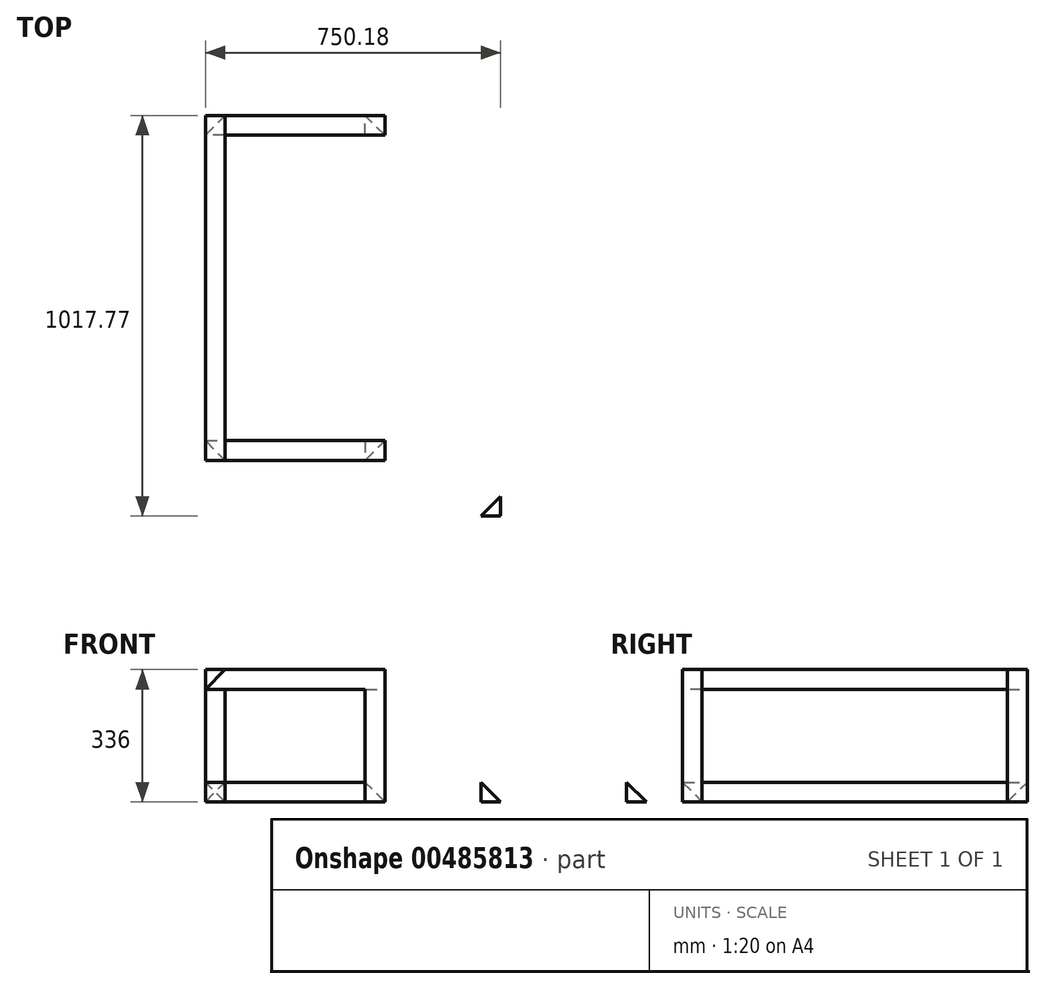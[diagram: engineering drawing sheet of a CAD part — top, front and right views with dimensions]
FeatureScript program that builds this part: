
annotation { "Feature Type Name" : "Feature", "Feature Type Description" : "" }
export const myFeature = defineFeature(function(context is Context, id is Id, definition is map)
    precondition{}
    {
        {
            var Q0;
            Q0=qCreatedBy(makeId("Top.planeOp"),FACE);
            var sketch = newSketch(context, id + "F0", { "sketchPlane" : qUnion([Q0])});
            skLineSegment(sketch, "E0.bottom", {"start": v(-25, 388) * mm, "end": v(25, 388) * mm});
            skLineSegment(sketch, "E0.top", {"start": v(-25, -388) * mm, "end": v(25, -388) * mm});
            skLineSegment(sketch, "E0.left", {"start": v(-25, 388) * mm, "end": v(-25, -388) * mm});
            skLineSegment(sketch, "E0.right", {"start": v(25, 388) * mm, "end": v(25, -388) * mm});
            skPoint(sketch, "E0.middle", {"position": v(0, 0) * mm});
            skSolve(sketch);
        }
        {
            var Q0;
            Q0 = qSketchRegion(id + "F0", true);
            extrude(context, id + "F1", {"entities" : qUnion([Q0]), "depth" : 50 * mm});
        }
        {
            var Q0;
            Q0=makeQuery(id+"F1.opExtrude","CAP_FACE",FACE,{"disambiguationData":[OSD([sQuery(id+"F0.wireOp",EDGE,"E0.bottom"),sQuery(id+"F0.wireOp",EDGE,"E0.top"),sQuery(id+"F0.wireOp",EDGE,"E0.left"),sQuery(id+"F0.wireOp",EDGE,"E0.right")])],"isStart":false});
            var sketch = newSketch(context, id + "F2", { "sketchPlane" : qUnion([Q0])});
            skLineSegment(sketch, "E1.top", {"start": v(-25, -438) * mm, "end": v(25, -438) * mm});
            skLineSegment(sketch, "E1.left", {"start": v(-25, -388) * mm, "end": v(-25, -438) * mm});
            skLineSegment(sketch, "E2.top", {"start": v(-25, 438) * mm, "end": v(25, 438) * mm});
            skLineSegment(sketch, "E2.left", {"start": v(-25, 388) * mm, "end": v(-25, 438) * mm});
            skLineSegment(sketch, "E3", {"start": v(25, -438) * mm, "end": v(-25, -388) * mm});
            skLineSegment(sketch, "E4", {"start": v(-25, 388) * mm, "end": v(25, 438) * mm});
            skSolve(sketch);
        }
        {
            var Q0;
            Q0 = qSketchRegion(id + "F2", true);
            extrude(context, id + "F3", {"entities" : qUnion([Q0]), "depth" : 236 * mm, "offsetDistance" : 25 * mm});
        }
        {
            var Q0;
            Q0=makeQuery(id+"F1.opExtrude","SWEPT_FACE",FACE,{"disambiguationData":[OSD([sQuery(id+"F0.wireOp",EDGE,"E0.right")])]});
            var sketch = newSketch(context, id + "F4", { "sketchPlane" : qUnion([Q0])});
            skLineSegment(sketch, "E5.bottom", {"start": v(-388, 0) * mm, "end": v(-438, 0) * mm});
            skLineSegment(sketch, "E5.right", {"start": v(-438, 0) * mm, "end": v(-438, 50) * mm});
            skLineSegment(sketch, "E6.bottom", {"start": v(388, 0) * mm, "end": v(438, 0) * mm});
            skLineSegment(sketch, "E6.right", {"start": v(438, 0) * mm, "end": v(438, 50) * mm});
            skLineSegment(sketch, "E7", {"start": v(-438, 50) * mm, "end": v(-388, 0) * mm});
            skLineSegment(sketch, "E8", {"start": v(388, 0) * mm, "end": v(438, 50) * mm});
            skSolve(sketch);
        }
        {
            var Q0;
            Q0 = qSketchRegion(id + "F4", true);
            extrude(context, id + "F5", {"entities" : qUnion([Q0]), "depth" : 356 * mm});
        }
        {
            var Q0;
            Q0=makeQuery(id+"F1.opExtrude","SWEPT_FACE",FACE,{"disambiguationData":[OSD([sQuery(id+"F0.wireOp",EDGE,"E0.bottom")])]});
            var sketch = newSketch(context, id + "F6", { "sketchPlane" : qUnion([Q0])});
            skLineSegment(sketch, "E9", {"start": v(-25, 0) * mm, "end": v(25, 50) * mm});
            skLineSegment(sketch, "E10", {"start": v(25, 50) * mm, "end": v(-25, 50) * mm});
            skLineSegment(sketch, "E11", {"start": v(-25, 50) * mm, "end": v(-25, 0) * mm});
            skSolve(sketch);
        }
        {
            var Q0;
            Q0=makeQuery(id+"F6.imprint","IMPRINT",FACE,{"disambiguationData":[TD([[makeQuery(id+"F6.imprint","IMPRINT",EDGE,{"derivedFrom":sQuery(id+"F6.wireOp",EDGE,"E9")}),1.0]])]});
            extrude(context, id + "F7", {"entities" : qUnion([Q0]), "operationType" : NewBodyOperationType.REMOVE, "oppositeDirection" : true, "depth" : 800 * mm});
        }
        {
            var Q0;
            Q0=makeQuery(id+"F5.opExtrude","SWEPT_FACE",FACE,{"disambiguationData":[OSD([sQuery(id+"F4.wireOp",EDGE,"E5.bottom")])]});
            var sketch = newSketch(context, id + "F8", { "sketchPlane" : qUnion([Q0])});
            skLineSegment(sketch, "E12.bottom", {"start": v(381, 438) * mm, "end": v(431, 438) * mm});
            skLineSegment(sketch, "E12.right", {"start": v(431, 438) * mm, "end": v(431, 388) * mm});
            skLineSegment(sketch, "E13", {"start": v(381, 438) * mm, "end": v(431, 388) * mm});
            skSolve(sketch);
        }
        {
            var Q0;
            Q0 = qSketchRegion(id + "F8", true);
            var Q1;
            Q1=makeQuery(id+"F3.opExtrude","CAP_FACE",FACE,{"disambiguationData":[OSD([sQuery(id+"F2.wireOp",EDGE,"E1.top"),sQuery(id+"F2.wireOp",EDGE,"E1.left"),sQuery(id+"F2.wireOp",EDGE,"E3")])],"isStart":false});
            extrude(context, id + "F9", {"entities" : qUnion([Q0]), "endBound" : BoundingType.UP_TO_SURFACE, "oppositeDirection" : true, "endBoundEntityFace" : qUnion([Q1]), "depth" : 25 * mm});
        }
        {
            var Q0;
            Q0=makeQuery(id+"F5.opExtrude","SWEPT_FACE",FACE,{"disambiguationData":[OSD([sQuery(id+"F4.wireOp",EDGE,"E6.bottom")])]});
            var sketch = newSketch(context, id + "F10", { "sketchPlane" : qUnion([Q0])});
            skLineSegment(sketch, "E14.bottom", {"start": v(381, -438) * mm, "end": v(431, -438) * mm});
            skLineSegment(sketch, "E14.right", {"start": v(431, -438) * mm, "end": v(431, -388) * mm});
            skLineSegment(sketch, "E15", {"start": v(381, -438) * mm, "end": v(431, -388) * mm});
            skSolve(sketch);
        }
        {
            var Q0;
            Q0 = qSketchRegion(id + "F10", true);
            var Q1;
            Q1=makeQuery(id+"F3.opExtrude","CAP_FACE",FACE,{"disambiguationData":[OSD([sQuery(id+"F2.wireOp",EDGE,"E2.top"),sQuery(id+"F2.wireOp",EDGE,"E2.left"),sQuery(id+"F2.wireOp",EDGE,"E4")])],"isStart":false});
            extrude(context, id + "F11", {"entities" : qUnion([Q0]), "endBound" : BoundingType.UP_TO_SURFACE, "oppositeDirection" : true, "endBoundEntityFace" : qUnion([Q1]), "depth" : 25 * mm});
        }
        {
            var Q0;
            Q0=makeQuery(id+"F3.opExtrude","CAP_FACE",FACE,{"disambiguationData":[OSD([sQuery(id+"F2.wireOp",EDGE,"E1.top"),sQuery(id+"F2.wireOp",EDGE,"E1.left"),sQuery(id+"F2.wireOp",EDGE,"E3")])],"isStart":false});
            var sketch = newSketch(context, id + "F12", { "sketchPlane" : qUnion([Q0])});
            skLineSegment(sketch, "E16.bottom", {"start": v(-25, -438) * mm, "end": v(25, -438) * mm});
            skLineSegment(sketch, "E16.top", {"start": v(-25, 438) * mm, "end": v(25, 438) * mm});
            skLineSegment(sketch, "E16.left", {"start": v(-25, -438) * mm, "end": v(-25, 438) * mm});
            skLineSegment(sketch, "E16.right", {"start": v(25, -438) * mm, "end": v(25, 438) * mm});
            skSolve(sketch);
        }
        {
            var Q0;
            Q0 = qSketchRegion(id + "F12", true);
            extrude(context, id + "F13", {"entities" : qUnion([Q0]), "depth" : 50 * mm});
        }
        {
            var Q0;
            Q0=makeQuery(id+"F13.opExtrude","SWEPT_FACE",FACE,{"disambiguationData":[OSD([sQuery(id+"F12.wireOp",EDGE,"E16.bottom")])]});
            var sketch = newSketch(context, id + "F14", { "sketchPlane" : qUnion([Q0])});
            skLineSegment(sketch, "E17", {"start": v(-25, 286) * mm, "end": v(25, 336) * mm});
            skLineSegment(sketch, "E18", {"start": v(-25, 286) * mm, "end": v(25, 286) * mm});
            skLineSegment(sketch, "E19", {"start": v(25, 286) * mm, "end": v(25, 336) * mm});
            skSolve(sketch);
        }
        {
            var Q0;
            Q0 = qSketchRegion(id + "F14", true);
            extrude(context, id + "F15", {"entities" : qUnion([Q0]), "operationType" : NewBodyOperationType.REMOVE, "oppositeDirection" : true, "depth" : 880 * mm});
        }
        {
            var Q0;
            Q0=makeQuery(id+"F11.opExtrude","SWEPT_FACE",FACE,{"disambiguationData":[OSD([sQuery(id+"F10.wireOp",EDGE,"E14.bottom")])]});
            var sketch = newSketch(context, id + "F16", { "sketchPlane" : qUnion([Q0])});
            skLineSegment(sketch, "E20", {"start": v(-431, 286) * mm, "end": v(-381, 286) * mm});
            skLineSegment(sketch, "E21", {"start": v(-381, 286) * mm, "end": v(-381, 336) * mm});
            skLineSegment(sketch, "E22", {"start": v(-381, 336) * mm, "end": v(-431, 286) * mm});
            skSolve(sketch);
        }
        {
            var Q0;
            Q0 = qSketchRegion(id + "F16", true);
            extrude(context, id + "F17", {"entities" : qUnion([Q0]), "oppositeDirection" : true, "depth" : 50 * mm});
        }
        {
            var Q0;
            Q0=makeQuery(id+"F17.opExtrude","SWEPT_FACE",FACE,{"disambiguationData":[OSD([sQuery(id+"F16.wireOp",EDGE,"E21")])]});
            extrude(context, id + "F18", {"entities" : qUnion([Q0]), "endBound" : BoundingType.UP_TO_NEXT, "depth" : 25 * mm});
        }
        {
            var Q0;
            Q0=makeQuery(id+"F17.opExtrude","SWEPT_BODY",BODY,{"disambiguationData":[OSD([sQuery(id+"F16.wireOp",EDGE,"E20"),sQuery(id+"F16.wireOp",EDGE,"E21"),sQuery(id+"F16.wireOp",EDGE,"E22")])]});
            var Q1;
            Q1=makeQuery(id+"F18.opExtrude","SWEPT_BODY",BODY,{"disambiguationData":[OSD([sQuery(id+"F16.wireOp",EDGE,"E21")])]});
            booleanBodies(context, id + "F19", {"operationType" : BooleanOperationType.UNION, "tools" : qUnion([Q0, Q1])});
        }
        {
            var Q0;
            Q0=makeQuery(id+"F9.opExtrude","SWEPT_FACE",FACE,{"disambiguationData":[OSD([sQuery(id+"F8.wireOp",EDGE,"E12.bottom")])]});
            var sketch = newSketch(context, id + "F20", { "sketchPlane" : qUnion([Q0])});
            skLineSegment(sketch, "E23", {"start": v(431, 286) * mm, "end": v(381, 286) * mm});
            skLineSegment(sketch, "E24", {"start": v(381, 286) * mm, "end": v(381, 336) * mm});
            skLineSegment(sketch, "E25", {"start": v(381, 336) * mm, "end": v(431, 286) * mm});
            skSolve(sketch);
        }
        {
            var Q0;
            Q0 = qSketchRegion(id + "F20", true);
            extrude(context, id + "F21", {"entities" : qUnion([Q0]), "oppositeDirection" : true, "depth" : 50 * mm});
        }
        {
            var Q0;
            Q0=makeQuery(id+"F21.opExtrude","SWEPT_FACE",FACE,{"disambiguationData":[OSD([sQuery(id+"F20.wireOp",EDGE,"E24")])]});
            extrude(context, id + "F22", {"entities" : qUnion([Q0]), "endBound" : BoundingType.UP_TO_NEXT, "depth" : 25 * mm});
        }
        {
            var Q0;
            Q0=makeQuery(id+"F21.opExtrude","SWEPT_BODY",BODY,{"disambiguationData":[OSD([sQuery(id+"F20.wireOp",EDGE,"E23"),sQuery(id+"F20.wireOp",EDGE,"E24"),sQuery(id+"F20.wireOp",EDGE,"E25")])]});
            var Q1;
            Q1=makeQuery(id+"F22.opExtrude","SWEPT_BODY",BODY,{"disambiguationData":[OSD([sQuery(id+"F20.wireOp",EDGE,"E24")])]});
            booleanBodies(context, id + "F23", {"operationType" : BooleanOperationType.UNION, "tools" : qUnion([Q0, Q1])});
        }
        {
            var Q0;
            Q0=makeQuery(id+"F5.opExtrude","CAP_FACE",FACE,{"disambiguationData":[OSD([sQuery(id+"F4.wireOp",EDGE,"E6.bottom"),sQuery(id+"F4.wireOp",EDGE,"E6.right"),sQuery(id+"F4.wireOp",EDGE,"E8")])],"isStart":false});
            var Q1;
            Q1=makeQuery(id+"F5.opExtrude","CAP_FACE",FACE,{"disambiguationData":[OSD([sQuery(id+"F4.wireOp",EDGE,"E5.bottom"),sQuery(id+"F4.wireOp",EDGE,"E5.right"),sQuery(id+"F4.wireOp",EDGE,"E7")])],"isStart":false});
            extrude(context, id + "F24", {"entities" : qUnion([Q0, Q1]), "endBound" : BoundingType.UP_TO_NEXT, "depth" : 25 * mm});
        }
        {
            var Q0;
            Q0=makeQuery(id+"F3.opExtrude","CAP_FACE",FACE,{"disambiguationData":[OSD([sQuery(id+"F2.wireOp",EDGE,"E2.top"),sQuery(id+"F2.wireOp",EDGE,"E2.left"),sQuery(id+"F2.wireOp",EDGE,"E4")])],"isStart":true});
            var Q1;
            Q1=makeQuery(id+"F3.opExtrude","CAP_FACE",FACE,{"disambiguationData":[OSD([sQuery(id+"F2.wireOp",EDGE,"E1.top"),sQuery(id+"F2.wireOp",EDGE,"E1.left"),sQuery(id+"F2.wireOp",EDGE,"E3")])],"isStart":true});
            var Q2;
            Q2=makeQuery(id+"F1.opExtrude","CAP_FACE",FACE,{"disambiguationData":[OSD([sQuery(id+"F0.wireOp",EDGE,"E0.bottom"),sQuery(id+"F0.wireOp",EDGE,"E0.top"),sQuery(id+"F0.wireOp",EDGE,"E0.left"),sQuery(id+"F0.wireOp",EDGE,"E0.right")])],"isStart":true});
            extrude(context, id + "F25", {"entities" : qUnion([Q0, Q1]), "endBound" : BoundingType.UP_TO_SURFACE, "endBoundEntityFace" : qUnion([Q2]), "depth" : 25 * mm});
        }
        {
            var Q0;
            Q0=makeQuery(id+"F5.opExtrude","CAP_FACE",FACE,{"disambiguationData":[OSD([sQuery(id+"F4.wireOp",EDGE,"E5.bottom"),sQuery(id+"F4.wireOp",EDGE,"E5.right"),sQuery(id+"F4.wireOp",EDGE,"E7")])],"isStart":true});
            var Q1;
            Q1=makeQuery(id+"F5.opExtrude","CAP_FACE",FACE,{"disambiguationData":[OSD([sQuery(id+"F4.wireOp",EDGE,"E6.bottom"),sQuery(id+"F4.wireOp",EDGE,"E6.right"),sQuery(id+"F4.wireOp",EDGE,"E8")])],"isStart":true});
            extrude(context, id + "F26", {"entities" : qUnion([Q0, Q1]), "endBound" : BoundingType.UP_TO_NEXT, "depth" : 25 * mm});
        }
        {
            var Q0;
            {var subQ0=sQuery(id+"F20.wireOp",EDGE,"E24");Q0=makeQuery(id+"F23.opBoolean","MERGE",FACE,{"derivedFrom":[makeQuery(id+"F21.opExtrude","CAP_FACE",FACE,{"disambiguationData":[OSD([sQuery(id+"F20.wireOp",EDGE,"E23"),subQ0,sQuery(id+"F20.wireOp",EDGE,"E25")])],"isStart":true}),makeQuery(id+"F22.opExtrude","SWEPT_FACE",FACE,{"disambiguationData":[OSD([subQ0]),TDD([makeQuery(id+"F21.opExtrude","CAP_EDGE",EDGE,{"disambiguationData":[OSD([subQ0])],"isStart":true})])]})]});}
            var sketch = newSketch(context, id + "F27", { "sketchPlane" : qUnion([Q0])});
            skLineSegment(sketch, "E26", {"start": v(381, 336) * mm, "end": v(431, 286) * mm});
            skLineSegment(sketch, "E27", {"start": v(431, 286) * mm, "end": v(431, 336) * mm});
            skLineSegment(sketch, "E28", {"start": v(431, 336) * mm, "end": v(381, 336) * mm});
            skSolve(sketch);
        }
        {
            var Q0;
            Q0 = qSketchRegion(id + "F27", true);
            var Q1;
            {var subQ0=sQuery(id+"F20.wireOp",EDGE,"E24");Q1=makeQuery(id+"F23.opBoolean","MERGE",FACE,{"derivedFrom":[makeQuery(id+"F21.opExtrude","CAP_FACE",FACE,{"disambiguationData":[OSD([sQuery(id+"F20.wireOp",EDGE,"E23"),subQ0,sQuery(id+"F20.wireOp",EDGE,"E25")])],"isStart":false}),makeQuery(id+"F22.opExtrude","SWEPT_FACE",FACE,{"disambiguationData":[OSD([subQ0]),TDD([makeQuery(id+"F21.opExtrude","CAP_EDGE",EDGE,{"disambiguationData":[OSD([subQ0])],"isStart":false})])]})]});}
            extrude(context, id + "F28", {"entities" : qUnion([Q0]), "operationType" : NewBodyOperationType.ADD, "endBound" : BoundingType.UP_TO_SURFACE, "oppositeDirection" : true, "depth" : 25 * mm, "endBoundEntityFace" : qUnion([Q1]), "offsetDistance" : 25 * mm});
        }
        {
            var Q0;
            {var subQ0=sQuery(id+"F16.wireOp",EDGE,"E21");Q0=makeQuery(id+"F19.opBoolean","MERGE",FACE,{"derivedFrom":[makeQuery(id+"F17.opExtrude","CAP_FACE",FACE,{"disambiguationData":[OSD([sQuery(id+"F16.wireOp",EDGE,"E20"),subQ0,sQuery(id+"F16.wireOp",EDGE,"E22")])],"isStart":true}),makeQuery(id+"F18.opExtrude","SWEPT_FACE",FACE,{"disambiguationData":[OSD([subQ0]),TDD([makeQuery(id+"F17.opExtrude","CAP_EDGE",EDGE,{"disambiguationData":[OSD([subQ0])],"isStart":true})])]})]});}
            var sketch = newSketch(context, id + "F29", { "sketchPlane" : qUnion([Q0])});
            skLineSegment(sketch, "E29", {"start": v(-431, 286) * mm, "end": v(-431, 336) * mm});
            skLineSegment(sketch, "E30", {"start": v(-431, 336) * mm, "end": v(-381, 336) * mm});
            skLineSegment(sketch, "E31", {"start": v(-381, 336) * mm, "end": v(-431, 286) * mm});
            skSolve(sketch);
        }
        {
            var Q0;
            Q0 = qSketchRegion(id + "F29", true);
            var Q1;
            {var subQ0=sQuery(id+"F16.wireOp",EDGE,"E21");Q1=makeQuery(id+"F19.opBoolean","MERGE",FACE,{"derivedFrom":[makeQuery(id+"F17.opExtrude","CAP_FACE",FACE,{"disambiguationData":[OSD([sQuery(id+"F16.wireOp",EDGE,"E20"),subQ0,sQuery(id+"F16.wireOp",EDGE,"E22")])],"isStart":false}),makeQuery(id+"F18.opExtrude","SWEPT_FACE",FACE,{"disambiguationData":[OSD([subQ0]),TDD([makeQuery(id+"F17.opExtrude","CAP_EDGE",EDGE,{"disambiguationData":[OSD([subQ0])],"isStart":false})])]})]});}
            extrude(context, id + "F30", {"entities" : qUnion([Q0]), "operationType" : NewBodyOperationType.ADD, "endBound" : BoundingType.UP_TO_SURFACE, "oppositeDirection" : true, "depth" : 25 * mm, "endBoundEntityFace" : qUnion([Q1]), "offsetDistance" : 25 * mm});
        }
        {
            var Q0;
            Q0=qCreatedBy(makeId("Top.planeOp"),FACE);
            var sketch = newSketch(context, id + "F31", { "sketchPlane" : qUnion([Q0])});
            skLineSegment(sketch, "E32.bottom", {"start": v(675.18, -579.77) * mm, "end": v(725.18, -579.77) * mm});
            skLineSegment(sketch, "E32.top", {"start": v(675.18, -529.77) * mm, "end": v(725.18, -529.77) * mm});
            skLineSegment(sketch, "E32.left", {"start": v(675.18, -579.77) * mm, "end": v(675.18, -529.77) * mm});
            skLineSegment(sketch, "E32.right", {"start": v(725.18, -579.77) * mm, "end": v(725.18, -529.77) * mm});
            skLineSegment(sketch, "E33", {"start": v(675.18, -579.77) * mm, "end": v(725.18, -529.77) * mm});
            skLineSegment(sketch, "E34", {"start": v(725.18, -579.77) * mm, "end": v(675.18, -579.77) * mm, "construction": true});
            skLineSegment(sketch, "E35", {"start": v(675.18, -529.77) * mm, "end": v(725.18, -529.77) * mm, "construction": true});
            skSolve(sketch);
        }
        {
            var Q0;
            Q0 = qSketchRegion(id + "F31", true);
            extrude(context, id + "F32", {"entities" : qUnion([Q0]), "depth" : 50 * mm, "offsetDistance" : 25 * mm});
        }
        {
            var Q0;
            Q0=makeQuery(id+"F32.opExtrude","SWEPT_FACE",FACE,{"disambiguationData":[OSD([sQuery(id+"F31.wireOp",EDGE,"E32.top")])]});
            var sketch = newSketch(context, id + "F33", { "sketchPlane" : qUnion([Q0])});
            skLineSegment(sketch, "E36", {"start": v(-675.18, 50) * mm, "end": v(-725.18, 50) * mm});
            skLineSegment(sketch, "E37", {"start": v(-725.18, 50) * mm, "end": v(-725.18, 0) * mm});
            skLineSegment(sketch, "E38", {"start": v(-725.18, 0) * mm, "end": v(-675.18, 50) * mm});
            skSolve(sketch);
        }
        {
            var Q0;
            Q0=makeQuery(id+"F32.opExtrude","CAP_FACE",FACE,{"disambiguationData":[OSD([sQuery(id+"F31.wireOp",EDGE,"E32.bottom"),sQuery(id+"F31.wireOp",EDGE,"E32.top"),sQuery(id+"F31.wireOp",EDGE,"E32.left"),sQuery(id+"F31.wireOp",EDGE,"E32.right")])],"isStart":false});
            var sketch = newSketch(context, id + "F34", { "sketchPlane" : qUnion([Q0])});
            skLineSegment(sketch, "E39", {"start": v(675.18, -579.77) * mm, "end": v(725.18, -529.77) * mm});
            skLineSegment(sketch, "E40", {"start": v(725.18, -529.77) * mm, "end": v(675.18, -529.77) * mm});
            skLineSegment(sketch, "E41", {"start": v(675.18, -529.77) * mm, "end": v(675.18, -579.77) * mm});
            skSolve(sketch);
        }
        {
            var Q0;
            Q0 = qSketchRegion(id + "F34", true);
            extrude(context, id + "F35", {"entities" : qUnion([Q0]), "operationType" : NewBodyOperationType.REMOVE, "oppositeDirection" : true, "depth" : 50 * mm, "offsetDistance" : 25 * mm});
        }
        {
            var Q0;
            Q0 = qSketchRegion(id + "F33", true);
            extrude(context, id + "F36", {"entities" : qUnion([Q0]), "operationType" : NewBodyOperationType.REMOVE, "oppositeDirection" : true, "depth" : 50 * mm, "offsetDistance" : 25 * mm});
        }
    });
